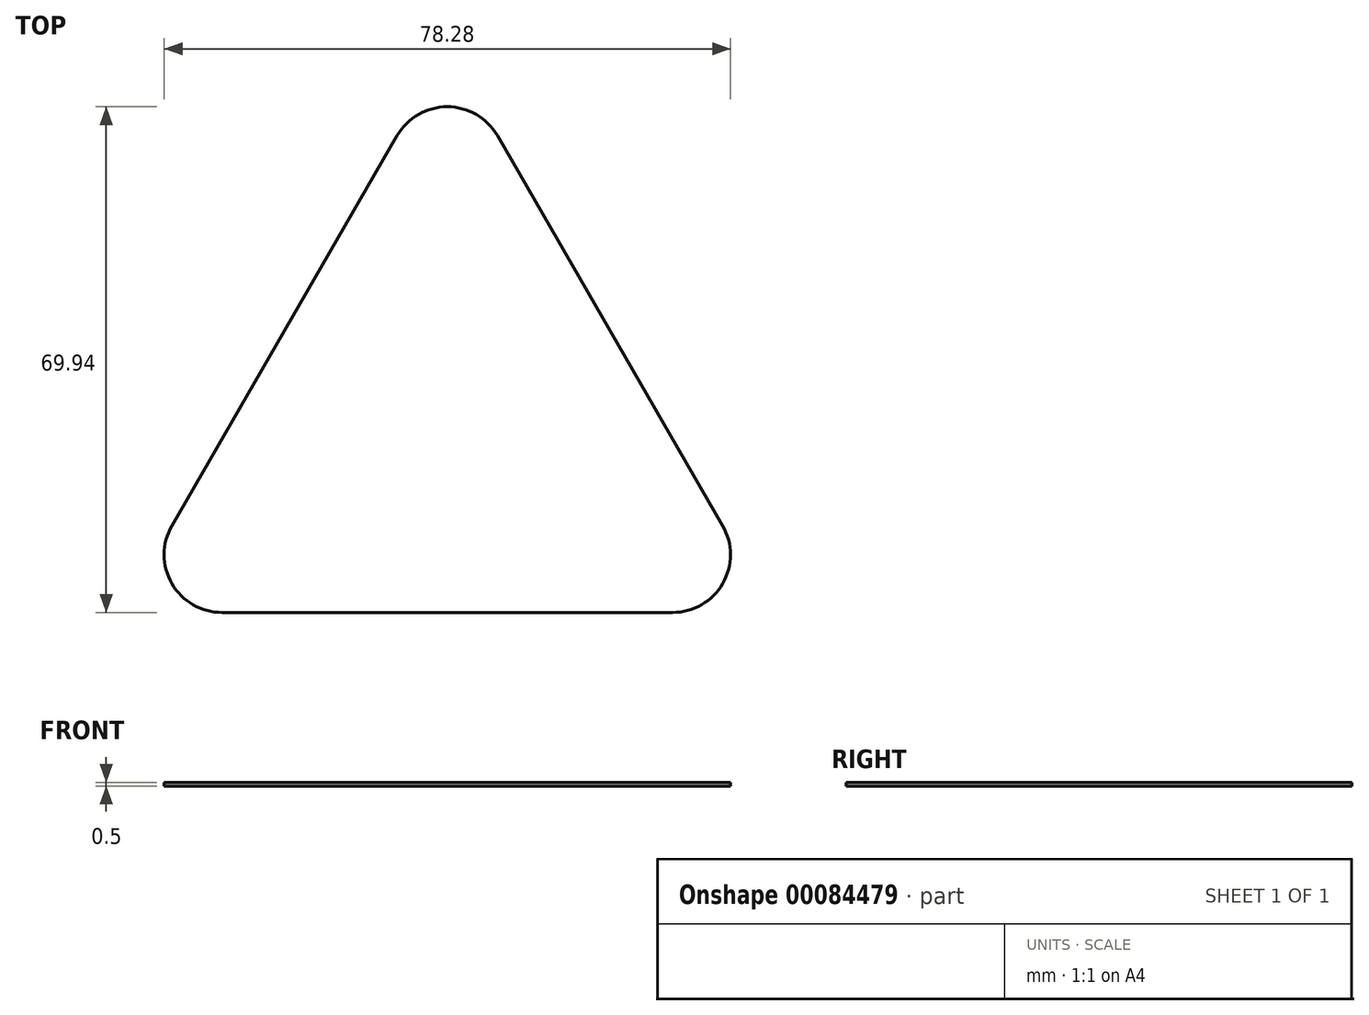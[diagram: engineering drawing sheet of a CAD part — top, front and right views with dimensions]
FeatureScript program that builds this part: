
annotation { "Feature Type Name" : "Feature", "Feature Type Description" : "" }
export const myFeature = defineFeature(function(context is Context, id is Id, definition is map)
    precondition{}
    {
        {
            var Q0;
            Q0=qCreatedBy(makeId("Top.planeOp"),FACE);
            var sketch = newSketch(context, id + "F0", { "sketchPlane" : qUnion([Q0])});
            skLineSegment(sketch, "E0", {"start": v(31.14, 0) * mm, "end": v(-31.14, 0) * mm});
            skLineSegment(sketch, "E1", {"start": v(38.07, 12) * mm, "end": v(6.93, 65.94) * mm});
            skLineSegment(sketch, "E2", {"start": v(-6.93, 65.94) * mm, "end": v(-38.07, 12) * mm});
            skPoint(sketch, "E3.visualSharp", {"position": v(0, 77.94) * mm});
            skArc(sketch, "E3.filletArc", {"start": v(6.93, 65.94) * mm, "mid": v(0, 69.94) * mm, "end": v(-6.93, 65.94) * mm});
            skPoint(sketch, "E4.visualSharp", {"position": v(-45, 0) * mm});
            skArc(sketch, "E4.filletArc", {"start": v(-38.07, 12) * mm, "mid": v(-38.07, 4) * mm, "end": v(-31.14, 0) * mm});
            skPoint(sketch, "E5.visualSharp", {"position": v(45, 0) * mm});
            skArc(sketch, "E5.filletArc", {"start": v(31.14, 0) * mm, "mid": v(38.07, 4) * mm, "end": v(38.07, 12) * mm});
            skSolve(sketch);
        }
        {
            var Q0;
            Q0 = qSketchRegion(id + "F0", true);
            extrude(context, id + "F1", {"entities" : qUnion([Q0]), "depth" : 0.5 * mm});
        }
    });
